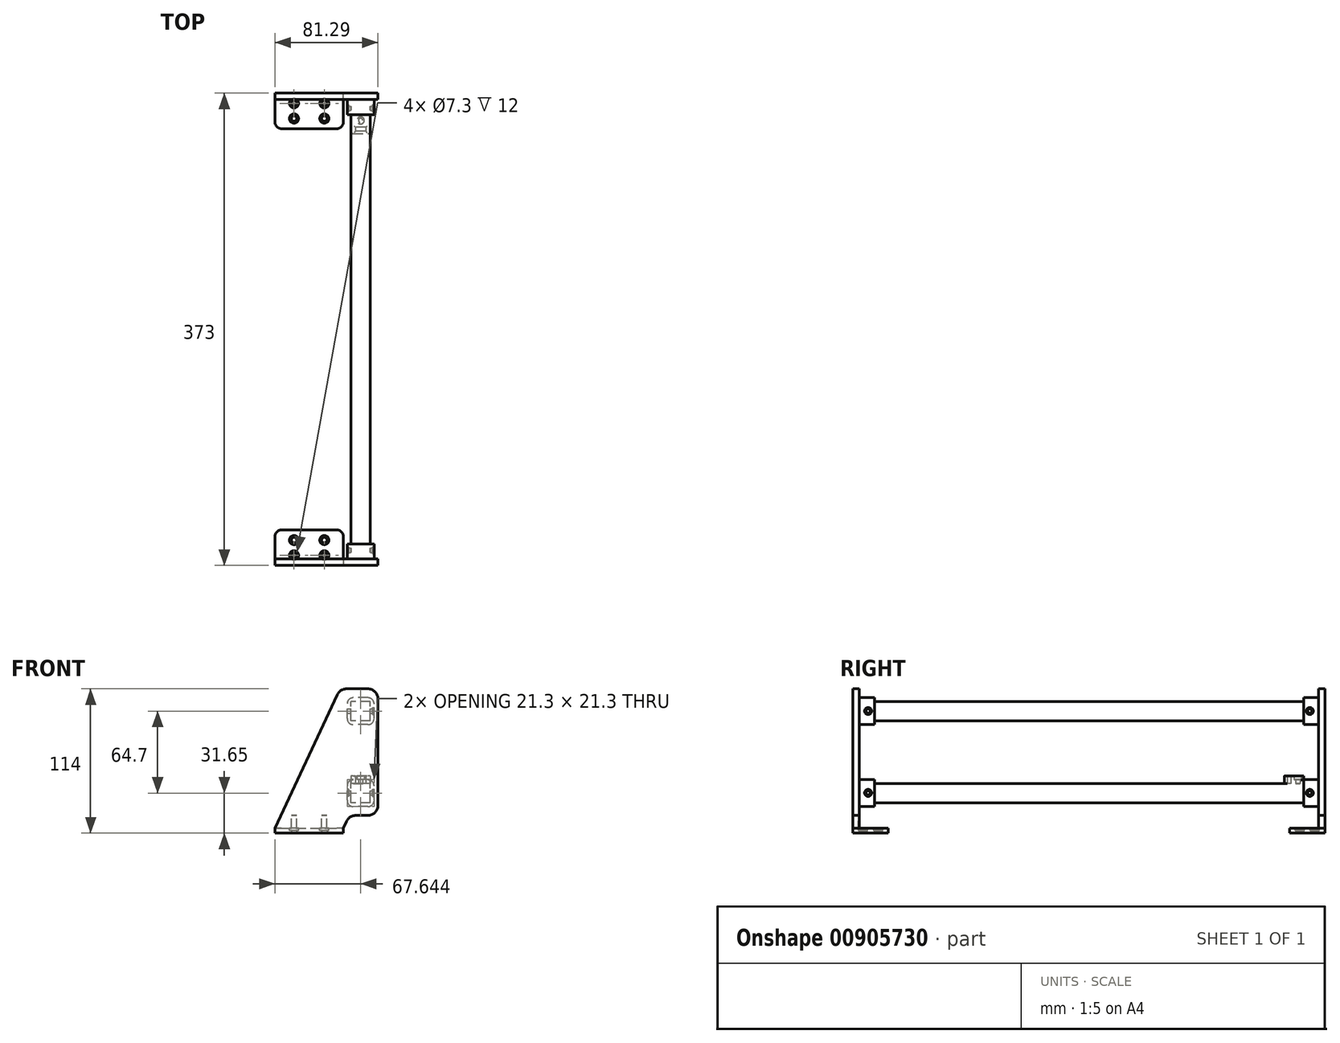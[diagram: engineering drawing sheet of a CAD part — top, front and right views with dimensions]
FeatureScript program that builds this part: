
annotation { "Feature Type Name" : "Feature", "Feature Type Description" : "" }
export const myFeature = defineFeature(function(context is Context, id is Id, definition is map)
    precondition{}
    {
        {
            var Q0;
            Q0=qCreatedBy(makeId("Top.planeOp"),FACE);
            var sketch = newSketch(context, id + "F0", { "sketchPlane" : qUnion([Q0])});
            skLineSegment(sketch, "E0.bottom", {"start": v(-27, 14) * mm, "end": v(27, 14) * mm});
            skLineSegment(sketch, "E0.top", {"start": v(-27, -14) * mm, "end": v(27, -14) * mm});
            skLineSegment(sketch, "E0.left", {"start": v(-27, 14) * mm, "end": v(-27, -14) * mm});
            skLineSegment(sketch, "E0.right", {"start": v(27, 14) * mm, "end": v(27, -14) * mm});
            skPoint(sketch, "E0.middle", {"position": v(0, 0) * mm});
            skCircle(sketch, "E1", {"center": v(-12, -6) * mm, "radius": 2.15 * mm});
            skCircle(sketch, "E2", {"center": v(12, -6) * mm, "radius": 2.15 * mm});
            skCircle(sketch, "E3", {"center": v(-12, 6) * mm, "radius": 2.15 * mm});
            skCircle(sketch, "E4", {"center": v(12, 6) * mm, "radius": 2.15 * mm});
            skSolve(sketch);
        }
        {
            var Q0;
            Q0=makeQuery(id+"F0.imprint","IMPRINT",FACE,{"disambiguationData":[TD([[makeQuery(id+"F0.imprint","IMPRINT",EDGE,{"derivedFrom":sQuery(id+"F0.wireOp",EDGE,"E0.bottom")}),-1.0]])]});
            extrude(context, id + "F1", {"entities" : qUnion([Q0]), "depth" : 4 * mm, "offsetDistance" : 25 * mm});
        }
        {
            var Q0;
            Q0=makeQuery(id+"F1.opExtrude","SWEPT_FACE",FACE,{"disambiguationData":[OSD([sQuery(id+"F0.wireOp",EDGE,"E0.top")])]});
            var sketch = newSketch(context, id + "F2", { "sketchPlane" : qUnion([Q0])});
            skLineSegment(sketch, "E5", {"start": v(-27, 4) * mm, "end": v(24.3, 114) * mm});
            skLineSegment(sketch, "E6", {"start": v(54.3, 14) * mm, "end": v(54.3, 114) * mm});
            skLineSegment(sketch, "E7", {"start": v(54.3, 114) * mm, "end": v(24.3, 114) * mm});
            skLineSegment(sketch, "E8.bottom", {"start": v(48.3, 88.7) * mm, "end": v(33, 88.7) * mm});
            skLineSegment(sketch, "E8.top", {"start": v(48.3, 104) * mm, "end": v(33, 104) * mm});
            skLineSegment(sketch, "E8.left", {"start": v(48.3, 88.7) * mm, "end": v(48.3, 104) * mm});
            skLineSegment(sketch, "E8.right", {"start": v(33, 88.7) * mm, "end": v(33, 104) * mm});
            skPoint(sketch, "E8.middle", {"position": v(40.64, 96.35) * mm});
            skLineSegment(sketch, "E9.bottom", {"start": v(48.3, 24) * mm, "end": v(33, 24) * mm});
            skLineSegment(sketch, "E9.top", {"start": v(48.3, 39.3) * mm, "end": v(33, 39.3) * mm});
            skLineSegment(sketch, "E9.left", {"start": v(48.3, 24) * mm, "end": v(48.3, 39.3) * mm});
            skLineSegment(sketch, "E9.right", {"start": v(33, 24) * mm, "end": v(33, 39.3) * mm});
            skPoint(sketch, "E9.middle", {"position": v(40.64, 31.65) * mm});
            skLineSegment(sketch, "E10", {"start": v(54.3, 14) * mm, "end": v(31.66, 14) * mm});
            skLineSegment(sketch, "E11", {"start": v(31.66, 14) * mm, "end": v(27, 4) * mm});
            skLineSegment(sketch, "E12", {"start": v(-27, 4) * mm, "end": v(27, 4) * mm});
            skSolve(sketch);
        }
        {
            var Q0;
            Q0=makeQuery(id+"F2.imprint","IMPRINT",FACE,{"disambiguationData":[TD([[makeQuery(id+"F2.imprint","IMPRINT",EDGE,{"derivedFrom":sQuery(id+"F2.wireOp",EDGE,"E5")}),-1.0]])]});
            var Q1;
            Q1=makeQuery(id+"F2.imprint","IMPRINT",FACE,{"disambiguationData":[TD([[makeQuery(id+"F2.imprint","IMPRINT",EDGE,{"derivedFrom":sQuery(id+"F2.wireOp",EDGE,"E8.bottom")}),-1.0]])]});
            var Q2;
            Q2=makeQuery(id+"F2.imprint","IMPRINT",FACE,{"disambiguationData":[TD([[makeQuery(id+"F2.imprint","IMPRINT",EDGE,{"derivedFrom":sQuery(id+"F2.wireOp",EDGE,"E9.bottom")}),-1.0]])]});
            extrude(context, id + "F3", {"entities" : qUnion([Q0, Q1, Q2]), "operationType" : NewBodyOperationType.ADD, "oppositeDirection" : true, "depth" : 5 * mm, "offsetDistance" : 25 * mm});
        }
        {
            var Q0;
            Q0=makeQuery(id+"F3.opExtrude","SWEPT_EDGE",EDGE,{"disambiguationData":[OSD([sQuery(id+"F2.wireOp",EDGE,"E6"),sQuery(id+"F2.wireOp",EDGE,"E7")])]});
            var Q1;
            Q1=makeQuery(id+"F3.opExtrude","SWEPT_EDGE",EDGE,{"disambiguationData":[OSD([sQuery(id+"F2.wireOp",EDGE,"E6"),sQuery(id+"F2.wireOp",EDGE,"E10")])]});
            var Q2;
            Q2=makeQuery(id+"F3.opExtrude","SWEPT_EDGE",EDGE,{"disambiguationData":[OSD([sQuery(id+"F2.wireOp",EDGE,"E10"),sQuery(id+"F2.wireOp",EDGE,"E11")])]});
            var Q3;
            Q3=makeQuery(id+"F3.opExtrude","SWEPT_EDGE",EDGE,{"disambiguationData":[OSD([sQuery(id+"F2.wireOp",EDGE,"E5"),sQuery(id+"F2.wireOp",EDGE,"E7")])]});
            fillet(context, id + "F4", {"entities" : qUnion([Q0, Q1, Q2, Q3]), "radius" : 8 * mm, "tangentPropagation" : true, "allowEdgeOverflow" : false});
        }
        {
            var Q0;
            Q0=makeQuery(id+"F3.opExtrude","CAP_FACE",FACE,{"disambiguationData":[OSD([sQuery(id+"F2.wireOp",EDGE,"E5"),sQuery(id+"F2.wireOp",EDGE,"E6"),sQuery(id+"F2.wireOp",EDGE,"E7"),sQuery(id+"F2.wireOp",EDGE,"E10"),sQuery(id+"F2.wireOp",EDGE,"E11"),sQuery(id+"F2.wireOp",EDGE,"E12")])],"isStart":false});
            var sketch = newSketch(context, id + "F5", { "sketchPlane" : qUnion([Q0])});
            skLineSegment(sketch, "E13.0", {"start": v(-48.3, 104) * mm, "end": v(-33, 104) * mm});
            skLineSegment(sketch, "E14.0", {"start": v(-33, 88.7) * mm, "end": v(-33, 104) * mm});
            skLineSegment(sketch, "E15.0", {"start": v(-48.3, 88.7) * mm, "end": v(-33, 88.7) * mm});
            skLineSegment(sketch, "E16.0", {"start": v(-48.3, 88.7) * mm, "end": v(-48.3, 104) * mm});
            skLineSegment(sketch, "E17.0", {"start": v(-48.3, 39.3) * mm, "end": v(-33, 39.3) * mm});
            skLineSegment(sketch, "E18.0", {"start": v(-33, 24) * mm, "end": v(-33, 39.3) * mm});
            skLineSegment(sketch, "E19.0", {"start": v(-48.3, 24) * mm, "end": v(-33, 24) * mm});
            skPoint(sketch, "E20.0", {"position": v(-48.3, 31.65) * mm});
            skLineSegment(sketch, "E21.0", {"start": v(-48.3, 24) * mm, "end": v(-48.3, 39.3) * mm});
            skLineSegment(sketch, "E22.0", {"start": v(-51.3, 107) * mm, "end": v(-30, 107) * mm});
            skLineSegment(sketch, "E22.1", {"start": v(-51.3, 85.7) * mm, "end": v(-51.3, 107) * mm});
            skLineSegment(sketch, "E22.2", {"start": v(-51.3, 85.7) * mm, "end": v(-30, 85.7) * mm});
            skLineSegment(sketch, "E22.3", {"start": v(-30, 85.7) * mm, "end": v(-30, 107) * mm});
            skLineSegment(sketch, "E23.0", {"start": v(-51.3, 42.3) * mm, "end": v(-30, 42.3) * mm});
            skLineSegment(sketch, "E23.1", {"start": v(-51.3, 21) * mm, "end": v(-51.3, 42.3) * mm});
            skLineSegment(sketch, "E23.2", {"start": v(-51.3, 21) * mm, "end": v(-30, 21) * mm});
            skLineSegment(sketch, "E23.3", {"start": v(-30, 21) * mm, "end": v(-30, 42.3) * mm});
            skSolve(sketch);
        }
        {
            var Q0;
            Q0=qCreatedBy(makeId("Front.planeOp"),FACE);
            var sketch = newSketch(context, id + "F6", { "sketchPlane" : qUnion([Q0])});
            skLineSegment(sketch, "E24.bottom", {"start": v(48.3, 104) * mm, "end": v(33, 104) * mm});
            skLineSegment(sketch, "E24.top", {"start": v(48.3, 88.7) * mm, "end": v(33, 88.7) * mm});
            skLineSegment(sketch, "E24.left", {"start": v(48.3, 104) * mm, "end": v(48.3, 88.7) * mm});
            skLineSegment(sketch, "E24.right", {"start": v(33, 104) * mm, "end": v(33, 88.7) * mm});
            skPoint(sketch, "E24.middle", {"position": v(40.64, 96.35) * mm});
            skLineSegment(sketch, "E25.bottom", {"start": v(48.3, 39.3) * mm, "end": v(33, 39.3) * mm});
            skLineSegment(sketch, "E25.top", {"start": v(48.3, 24) * mm, "end": v(33, 24) * mm});
            skLineSegment(sketch, "E25.left", {"start": v(48.3, 39.3) * mm, "end": v(48.3, 24) * mm});
            skLineSegment(sketch, "E25.right", {"start": v(33, 39.3) * mm, "end": v(33, 24) * mm});
            skPoint(sketch, "E25.middle", {"position": v(40.64, 31.65) * mm});
            skSolve(sketch);
        }
        {
            var Q0;
            Q0=makeQuery(id+"F6.imprint","IMPRINT",FACE,{"disambiguationData":[TD([[makeQuery(id+"F6.imprint","IMPRINT",EDGE,{"derivedFrom":sQuery(id+"F6.wireOp",EDGE,"E24.bottom")}),1.0]])]});
            var Q1;
            Q1=makeQuery(id+"F6.imprint","IMPRINT",FACE,{"disambiguationData":[TD([[makeQuery(id+"F6.imprint","IMPRINT",EDGE,{"derivedFrom":sQuery(id+"F6.wireOp",EDGE,"E25.bottom")}),1.0]])]});
            extrude(context, id + "F7", {"entities" : qUnion([Q0, Q1]), "depth" : 7.5 * mm, "offsetDistance" : 25 * mm, "hasSecondDirection" : true, "secondDirectionOppositeDirection" : true, "secondDirectionDepth" : (360 - 7.5) * mm});
        }
        {
            var Q0;
            Q0=makeQuery(id+"F5.imprint","IMPRINT",FACE,{"disambiguationData":[TD([[makeQuery(id+"F5.imprint","IMPRINT",EDGE,{"derivedFrom":sQuery(id+"F5.wireOp",EDGE,"E13.0")}),-1.0]])]});
            var Q1;
            Q1=makeQuery(id+"F5.imprint","IMPRINT",FACE,{"disambiguationData":[TD([[makeQuery(id+"F5.imprint","IMPRINT",EDGE,{"derivedFrom":sQuery(id+"F5.wireOp",EDGE,"E17.0")}),-1.0]])]});
            extrude(context, id + "F8", {"entities" : qUnion([Q0, Q1]), "operationType" : NewBodyOperationType.ADD, "depth" : 1.5 * mm, "offsetDistance" : 25 * mm});
        }
        {
            var Q0;
            Q0=makeQuery(id+"F5.imprint","IMPRINT",FACE,{"disambiguationData":[TD([[makeQuery(id+"F5.imprint","IMPRINT",EDGE,{"derivedFrom":sQuery(id+"F5.wireOp",EDGE,"E13.0")}),1.0]])]});
            var Q1;
            Q1=makeQuery(id+"F5.imprint","IMPRINT",FACE,{"disambiguationData":[TD([[makeQuery(id+"F5.imprint","IMPRINT",EDGE,{"derivedFrom":sQuery(id+"F5.wireOp",EDGE,"E17.0")}),1.0]])]});
            extrude(context, id + "F9", {"entities" : qUnion([Q0, Q1]), "operationType" : NewBodyOperationType.ADD, "depth" : 12 * mm, "offsetDistance" : 25 * mm});
        }
        {
            var Q0;
            Q0=makeQuery(id+"F9.opExtrude","SWEPT_FACE",FACE,{"disambiguationData":[OSD([sQuery(id+"F5.wireOp",EDGE,"E22.1")])]});
            var sketch = newSketch(context, id + "F10", { "sketchPlane" : qUnion([Q0])});
            skCircle(sketch, "E26", {"center": v(-2, 96.5) * mm, "radius": 2.8 * mm});
            skCircle(sketch, "E27", {"center": v(-2, 96.5) * mm, "radius": 1.65 * mm});
            skCircle(sketch, "E28", {"center": v(-2, 31.8) * mm, "radius": 2.8 * mm});
            skCircle(sketch, "E29", {"center": v(-2, 31.8) * mm, "radius": 1.65 * mm});
            skSolve(sketch);
        }
        {
            var Q0;
            Q0=makeQuery(id+"F10.imprint","IMPRINT",FACE,{"disambiguationData":[TD([[makeQuery(id+"F10.imprint","IMPRINT",EDGE,{"derivedFrom":sQuery(id+"F10.wireOp",EDGE,"E27")}),1.0]])]});
            var Q1;
            Q1=makeQuery(id+"F9.opExtrude","SWEPT_FACE",FACE,{"disambiguationData":[OSD([sQuery(id+"F5.wireOp",EDGE,"E22.3")])]});
            extrude(context, id + "F11", {"entities" : qUnion([Q0]), "operationType" : NewBodyOperationType.REMOVE, "endBound" : BoundingType.UP_TO_SURFACE, "oppositeDirection" : true, "depth" : 25 * mm, "endBoundEntityFace" : qUnion([Q1]), "offsetDistance" : 25 * mm});
        }
        {
            var Q0;
            Q0=makeQuery(id+"F10.imprint","IMPRINT",FACE,{"disambiguationData":[TD([[makeQuery(id+"F10.imprint","IMPRINT",EDGE,{"derivedFrom":sQuery(id+"F10.wireOp",EDGE,"E29")}),1.0]])]});
            var Q1;
            Q1=makeQuery(id+"F9.opExtrude","SWEPT_FACE",FACE,{"disambiguationData":[OSD([sQuery(id+"F5.wireOp",EDGE,"E23.3")])]});
            extrude(context, id + "F12", {"entities" : qUnion([Q0]), "operationType" : NewBodyOperationType.REMOVE, "endBound" : BoundingType.UP_TO_SURFACE, "oppositeDirection" : true, "depth" : 25 * mm, "endBoundEntityFace" : qUnion([Q1]), "offsetDistance" : 25 * mm});
        }
        {
            var Q0;
            Q0=makeQuery(id+"F10.imprint","IMPRINT",FACE,{"disambiguationData":[TD([[makeQuery(id+"F10.imprint","IMPRINT",EDGE,{"derivedFrom":sQuery(id+"F10.wireOp",EDGE,"E26")}),1.0]])]});
            var Q1;
            Q1=makeQuery(id+"F10.imprint","IMPRINT",FACE,{"disambiguationData":[TD([[makeQuery(id+"F10.imprint","IMPRINT",EDGE,{"derivedFrom":sQuery(id+"F10.wireOp",EDGE,"E28")}),1.0]])]});
            extrude(context, id + "F13", {"entities" : qUnion([Q0, Q1]), "operationType" : NewBodyOperationType.REMOVE, "oppositeDirection" : true, "depth" : 1 * mm, "offsetDistance" : 25 * mm});
        }
        {
            var Q0;
            Q0=makeQuery(id+"F9.opExtrude","SWEPT_FACE",FACE,{"disambiguationData":[OSD([sQuery(id+"F5.wireOp",EDGE,"E23.3")])]});
            var sketch = newSketch(context, id + "F14", { "sketchPlane" : qUnion([Q0])});
            skCircle(sketch, "E30", {"center": v(2, 31.8) * mm, "radius": 2.8 * mm});
            skCircle(sketch, "E31.0", {"center": v(2, 96.5) * mm, "radius": 1.65 * mm});
            skCircle(sketch, "E32", {"center": v(2, 96.5) * mm, "radius": 2.8 * mm});
            skSolve(sketch);
        }
        {
            var Q0;
            Q0=makeQuery(id+"F14.imprint","IMPRINT",FACE,{"disambiguationData":[TD([[makeQuery(id+"F14.imprint","IMPRINT",EDGE,{"derivedFrom":sQuery(id+"F14.wireOp",EDGE,"E30")}),1.0]])]});
            var Q1;
            Q1=makeQuery(id+"F14.imprint","IMPRINT",FACE,{"disambiguationData":[TD([[makeQuery(id+"F14.imprint","IMPRINT",EDGE,{"derivedFrom":sQuery(id+"F14.wireOp",EDGE,"E31.0")}),1.0]])]});
            extrude(context, id + "F15", {"entities" : qUnion([Q0, Q1]), "operationType" : NewBodyOperationType.REMOVE, "oppositeDirection" : true, "depth" : 1 * mm, "offsetDistance" : 25 * mm});
        }
        {
            var Q0;
            Q0=makeQuery(id+"F9.opExtrude","SWEPT_EDGE",EDGE,{"disambiguationData":[OSD([sQuery(id+"F5.wireOp",EDGE,"E22.0"),sQuery(id+"F5.wireOp",EDGE,"E22.1")])]});
            var Q1;
            Q1=makeQuery(id+"F9.opExtrude","SWEPT_EDGE",EDGE,{"disambiguationData":[OSD([sQuery(id+"F5.wireOp",EDGE,"E22.1"),sQuery(id+"F5.wireOp",EDGE,"E22.2")])]});
            var Q2;
            Q2=makeQuery(id+"F9.opExtrude","SWEPT_EDGE",EDGE,{"disambiguationData":[OSD([sQuery(id+"F5.wireOp",EDGE,"E22.0"),sQuery(id+"F5.wireOp",EDGE,"E22.3")])]});
            var Q3;
            Q3=makeQuery(id+"F9.opExtrude","SWEPT_EDGE",EDGE,{"disambiguationData":[OSD([sQuery(id+"F5.wireOp",EDGE,"E22.2"),sQuery(id+"F5.wireOp",EDGE,"E22.3")])]});
            var Q4;
            Q4=makeQuery(id+"F9.opExtrude","SWEPT_EDGE",EDGE,{"disambiguationData":[OSD([sQuery(id+"F5.wireOp",EDGE,"E23.0"),sQuery(id+"F5.wireOp",EDGE,"E23.3")])]});
            var Q5;
            Q5=makeQuery(id+"F9.opExtrude","SWEPT_EDGE",EDGE,{"disambiguationData":[OSD([sQuery(id+"F5.wireOp",EDGE,"E23.2"),sQuery(id+"F5.wireOp",EDGE,"E23.3")])]});
            var Q6;
            Q6=makeQuery(id+"F9.opExtrude","SWEPT_EDGE",EDGE,{"disambiguationData":[OSD([sQuery(id+"F5.wireOp",EDGE,"E23.0"),sQuery(id+"F5.wireOp",EDGE,"E23.1")])]});
            var Q7;
            Q7=makeQuery(id+"F9.opExtrude","SWEPT_EDGE",EDGE,{"disambiguationData":[OSD([sQuery(id+"F5.wireOp",EDGE,"E23.1"),sQuery(id+"F5.wireOp",EDGE,"E23.2")])]});
            fillet(context, id + "F16", {"entities" : qUnion([Q0, Q1, Q2, Q3, Q4, Q5, Q6, Q7]), "radius" : 5 * mm, "tangentPropagation" : true, "allowEdgeOverflow" : false});
        }
        {
            var Q0;
            Q0=makeQuery(id+"F1.opExtrude","CAP_FACE",FACE,{"disambiguationData":[OSD([sQuery(id+"F0.wireOp",EDGE,"E0.bottom"),sQuery(id+"F0.wireOp",EDGE,"E0.top"),sQuery(id+"F0.wireOp",EDGE,"E0.left"),sQuery(id+"F0.wireOp",EDGE,"E0.right"),sQuery(id+"F0.wireOp",EDGE,"E1"),sQuery(id+"F0.wireOp",EDGE,"E2"),sQuery(id+"F0.wireOp",EDGE,"E3"),sQuery(id+"F0.wireOp",EDGE,"E4")])],"isStart":false});
            var sketch = newSketch(context, id + "F17", { "sketchPlane" : qUnion([Q0])});
            skCircle(sketch, "E33", {"center": v(12, 6) * mm, "radius": 3.65 * mm});
            skCircle(sketch, "E34", {"center": v(12, -6) * mm, "radius": 3.65 * mm});
            skCircle(sketch, "E35", {"center": v(-12, 6) * mm, "radius": 3.65 * mm});
            skCircle(sketch, "E36", {"center": v(-12, -6) * mm, "radius": 3.65 * mm});
            skSolve(sketch);
        }
        {
            var Q0;
            Q0 = qSketchRegion(id + "F17", true);
            extrude(context, id + "F18", {"entities" : qUnion([Q0]), "operationType" : NewBodyOperationType.REMOVE, "oppositeDirection" : true, "depth" : 2 * mm, "offsetDistance" : 25 * mm, "hasSecondDirection" : true, "secondDirectionOppositeDirection" : false, "secondDirectionDepth" : 10 * mm});
        }
        {
            var Q0;
            Q0=makeQuery(id+"F1.opExtrude","SWEPT_EDGE",EDGE,{"disambiguationData":[OSD([sQuery(id+"F0.wireOp",EDGE,"E0.bottom"),sQuery(id+"F0.wireOp",EDGE,"E0.right")])]});
            var Q1;
            Q1=makeQuery(id+"F1.opExtrude","SWEPT_EDGE",EDGE,{"disambiguationData":[OSD([sQuery(id+"F0.wireOp",EDGE,"E0.bottom"),sQuery(id+"F0.wireOp",EDGE,"E0.left")])]});
            fillet(context, id + "F19", {"entities" : qUnion([Q0, Q1]), "radius" : 5 * mm, "tangentPropagation" : true, "allowEdgeOverflow" : false});
        }
        {
            var Q0;
            Q0=makeQuery(id+"F7.opExtrude","CAP_FACE",FACE,{"disambiguationData":[OSD([sQuery(id+"F6.wireOp",EDGE,"E24.bottom"),sQuery(id+"F6.wireOp",EDGE,"E24.top"),sQuery(id+"F6.wireOp",EDGE,"E24.left"),sQuery(id+"F6.wireOp",EDGE,"E24.right")])],"isStart":true});
            cPlane(context, id + "F20", {"entities" : qUnion([Q0]), "cplaneType" : CPlaneType.OFFSET, "offset" : (360 / 2) * mm, "oppositeDirection" : true, "width" : 150 * mm, "height" : 150 * mm});
        }
        {
            var Q0;
            Q0=makeQuery(id+"F1.opExtrude","SWEPT_BODY",BODY,{"disambiguationData":[OSD([sQuery(id+"F0.wireOp",EDGE,"E0.bottom"),sQuery(id+"F0.wireOp",EDGE,"E0.top"),sQuery(id+"F0.wireOp",EDGE,"E0.left"),sQuery(id+"F0.wireOp",EDGE,"E0.right"),sQuery(id+"F0.wireOp",EDGE,"E1"),sQuery(id+"F0.wireOp",EDGE,"E2"),sQuery(id+"F0.wireOp",EDGE,"E3"),sQuery(id+"F0.wireOp",EDGE,"E4")])]});
            var Q1;
            Q1=qCreatedBy(id+"F20.planeOp",FACE);
            mirror(context, id + "F21", {"entities" : qUnion([Q0]), "mirrorPlane" : qUnion([Q1])});
        }
        {
            var Q0;
            Q0=makeQuery(id+"F7.opExtrude","SWEPT_FACE",FACE,{"disambiguationData":[OSD([sQuery(id+"F6.wireOp",EDGE,"E25.bottom")])]});
            var sketch = newSketch(context, id + "F22", { "sketchPlane" : qUnion([Q0])});
            skLineSegment(sketch, "E37.bottom", {"start": v(33, 342) * mm, "end": v(48.3, 342) * mm});
            skLineSegment(sketch, "E37.top", {"start": v(33, 327) * mm, "end": v(48.3, 327) * mm});
            skLineSegment(sketch, "E37.left", {"start": v(33, 342) * mm, "end": v(33, 327) * mm});
            skLineSegment(sketch, "E37.right", {"start": v(48.3, 342) * mm, "end": v(48.3, 327) * mm});
            skLineSegment(sketch, "E38.bottom", {"start": v(44.64, 332) * mm, "end": v(36.64, 332) * mm});
            skLineSegment(sketch, "E38.top", {"start": v(44.64, 329) * mm, "end": v(36.64, 329) * mm});
            skLineSegment(sketch, "E38.left", {"start": v(44.64, 332) * mm, "end": v(44.64, 329) * mm});
            skLineSegment(sketch, "E38.right", {"start": v(36.64, 332) * mm, "end": v(36.64, 329) * mm});
            skCircle(sketch, "E39", {"center": v(40.64, 337.5) * mm, "radius": 2.85 * mm});
            skCircle(sketch, "E40", {"center": v(40.64, 337.5) * mm, "radius": 1.65 * mm});
            skSolve(sketch);
        }
        {
            var Q0;
            Q0=makeQuery(id+"F22.imprint","IMPRINT",FACE,{"disambiguationData":[TD([[makeQuery(id+"F22.imprint","IMPRINT",EDGE,{"derivedFrom":sQuery(id+"F22.wireOp",EDGE,"E37.bottom")}),-1.0]])]});
            extrude(context, id + "F23", {"entities" : qUnion([Q0]), "depth" : 6 * mm, "offsetDistance" : 25 * mm});
        }
        {
            var Q0;
            Q0=makeQuery(id+"F22.imprint","IMPRINT",FACE,{"disambiguationData":[TD([[makeQuery(id+"F22.imprint","IMPRINT",EDGE,{"derivedFrom":sQuery(id+"F22.wireOp",EDGE,"E39")}),1.0]])]});
            extrude(context, id + "F24", {"entities" : qUnion([Q0]), "operationType" : NewBodyOperationType.ADD, "depth" : 3 * mm, "offsetDistance" : 25 * mm});
        }
        {
            var Q0;
            Q0=makeQuery(id+"F23.opExtrude","SWEPT_EDGE",EDGE,{"disambiguationData":[OSD([sQuery(id+"F6.wireOp",EDGE,"E25.bottom"),sQuery(id+"F6.wireOp",EDGE,"E25.right"),sQuery(id+"F22.wireOp",EDGE,"E37.bottom"),sQuery(id+"F22.wireOp",EDGE,"E37.left")])]});
            var Q1;
            Q1=makeQuery(id+"F23.opExtrude","SWEPT_EDGE",EDGE,{"disambiguationData":[OSD([sQuery(id+"F6.wireOp",EDGE,"E25.bottom"),sQuery(id+"F6.wireOp",EDGE,"E25.right"),sQuery(id+"F22.wireOp",EDGE,"E37.top"),sQuery(id+"F22.wireOp",EDGE,"E37.left")])]});
            var Q2;
            Q2=makeQuery(id+"F23.opExtrude","SWEPT_EDGE",EDGE,{"disambiguationData":[OSD([sQuery(id+"F6.wireOp",EDGE,"E25.bottom"),sQuery(id+"F6.wireOp",EDGE,"E25.left"),sQuery(id+"F22.wireOp",EDGE,"E37.top"),sQuery(id+"F22.wireOp",EDGE,"E37.right")])]});
            var Q3;
            Q3=makeQuery(id+"F23.opExtrude","SWEPT_EDGE",EDGE,{"disambiguationData":[OSD([sQuery(id+"F6.wireOp",EDGE,"E25.bottom"),sQuery(id+"F6.wireOp",EDGE,"E25.left"),sQuery(id+"F22.wireOp",EDGE,"E37.bottom"),sQuery(id+"F22.wireOp",EDGE,"E37.right")])]});
            fillet(context, id + "F25", {"entities" : qUnion([Q0, Q1, Q2, Q3]), "radius" : 2 * mm, "tangentPropagation" : true, "allowEdgeOverflow" : false});
        }
        {
            var Q0;
            Q0=makeQuery(id+"F23.opExtrude","CAP_EDGE",EDGE,{"disambiguationData":[OSD([sQuery(id+"F22.wireOp",EDGE,"E38.left")])],"isStart":false});
            var Q1;
            Q1=makeQuery(id+"F23.opExtrude","CAP_EDGE",EDGE,{"disambiguationData":[OSD([sQuery(id+"F22.wireOp",EDGE,"E38.bottom")])],"isStart":false});
            var Q2;
            Q2=makeQuery(id+"F23.opExtrude","CAP_EDGE",EDGE,{"disambiguationData":[OSD([sQuery(id+"F22.wireOp",EDGE,"E38.top")])],"isStart":false});
            var Q3;
            Q3=makeQuery(id+"F23.opExtrude","CAP_EDGE",EDGE,{"disambiguationData":[OSD([sQuery(id+"F22.wireOp",EDGE,"E38.right")])],"isStart":false});
            var Q4;
            Q4=makeQuery(id+"F23.opExtrude","CAP_EDGE",EDGE,{"disambiguationData":[OSD([sQuery(id+"F22.wireOp",EDGE,"E38.left")])],"isStart":true});
            var Q5;
            Q5=makeQuery(id+"F23.opExtrude","CAP_EDGE",EDGE,{"disambiguationData":[OSD([sQuery(id+"F22.wireOp",EDGE,"E38.bottom")])],"isStart":true});
            var Q6;
            Q6=makeQuery(id+"F23.opExtrude","CAP_EDGE",EDGE,{"disambiguationData":[OSD([sQuery(id+"F22.wireOp",EDGE,"E38.right")])],"isStart":true});
            var Q7;
            Q7=makeQuery(id+"F23.opExtrude","CAP_EDGE",EDGE,{"disambiguationData":[OSD([sQuery(id+"F22.wireOp",EDGE,"E38.top")])],"isStart":true});
            fillet(context, id + "F26", {"entities" : qUnion([Q0, Q1, Q2, Q3, Q4, Q5, Q6, Q7]), "radius" : 1 * mm, "tangentPropagation" : true, "allowEdgeOverflow" : false});
        }
    });
